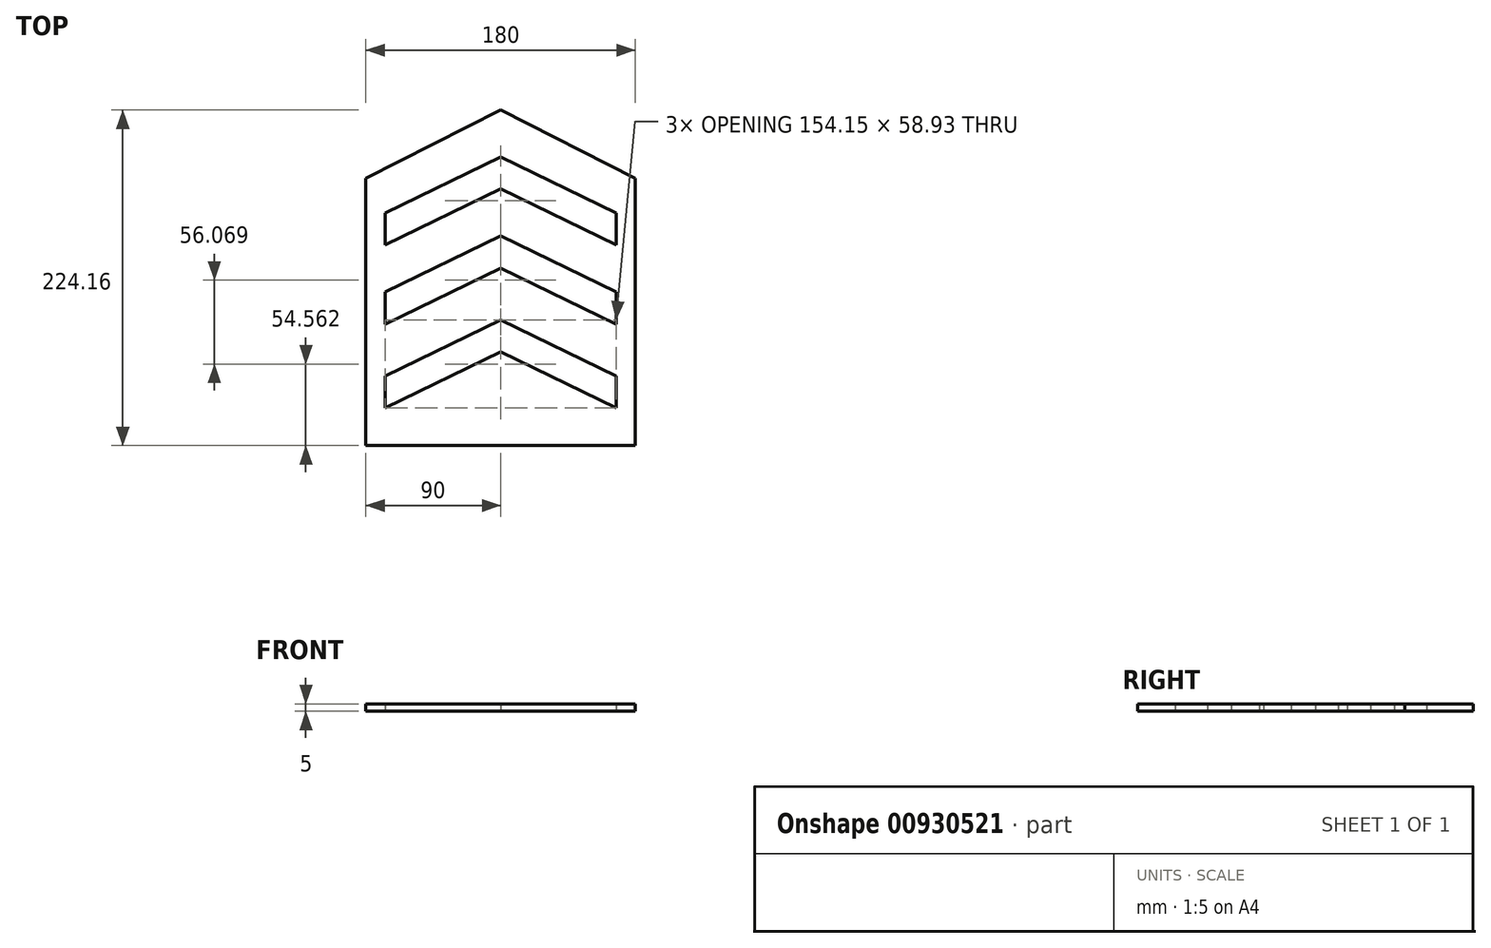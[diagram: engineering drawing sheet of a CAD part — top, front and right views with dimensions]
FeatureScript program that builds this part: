
annotation { "Feature Type Name" : "Feature", "Feature Type Description" : "" }
export const myFeature = defineFeature(function(context is Context, id is Id, definition is map)
    precondition{}
    {
        {
            var Q0;
            Q0=qCreatedBy(makeId("Top.planeOp"),FACE);
            var sketch = newSketch(context, id + "F0", { "sketchPlane" : qUnion([Q0])});
            skLineSegment(sketch, "E0", {"start": v(-447.88, 40.18) * mm, "end": v(-357.88, 85.93) * mm});
            skLineSegment(sketch, "E1", {"start": v(-447.88, 40.18) * mm, "end": v(-447.88, -138.23) * mm});
            skLineSegment(sketch, "E2.MirrorCS", {"start": v(-267.88, 40.18) * mm, "end": v(-357.88, 85.93) * mm});
            skLineSegment(sketch, "E3.MirrorCS", {"start": v(-267.88, 40.18) * mm, "end": v(-267.88, -138.23) * mm});
            skLineSegment(sketch, "E4", {"start": v(-447.88, -138.23) * mm, "end": v(-267.88, -138.23) * mm});
            skLineSegment(sketch, "E5.MirrorCS", {"start": v(-357.88, 54.77) * mm, "end": v(-280.8, 17.27) * mm});
            skLineSegment(sketch, "E6.MirrorCS", {"start": v(-280.8, 17.27) * mm, "end": v(-280.8, -4.16) * mm});
            skLineSegment(sketch, "E7.MirrorCS", {"start": v(-280.8, -4.16) * mm, "end": v(-357.88, 33.34) * mm});
            skLineSegment(sketch, "E8.MirrorCS", {"start": v(-357.88, 1.87) * mm, "end": v(-280.8, -35.64) * mm});
            skLineSegment(sketch, "E9.MirrorCS", {"start": v(-280.8, -57.07) * mm, "end": v(-357.88, -19.56) * mm});
            skLineSegment(sketch, "E10.MirrorCS", {"start": v(-357.88, -54.2) * mm, "end": v(-280.8, -91.7) * mm});
            skLineSegment(sketch, "E11.MirrorCS", {"start": v(-280.8, -113.13) * mm, "end": v(-357.88, -75.63) * mm});
            skLineSegment(sketch, "E12", {"start": v(-280.8, -35.64) * mm, "end": v(-280.8, -57.07) * mm});
            skLineSegment(sketch, "E13", {"start": v(-280.8, -91.7) * mm, "end": v(-280.8, -113.13) * mm});
            skLineSegment(sketch, "E14.MirrorCS", {"start": v(-357.88, 54.77) * mm, "end": v(-434.95, 17.27) * mm});
            skLineSegment(sketch, "E15.MirrorCS", {"start": v(-434.95, -4.16) * mm, "end": v(-357.88, 33.34) * mm});
            skLineSegment(sketch, "E16.MirrorCS", {"start": v(-434.95, 17.27) * mm, "end": v(-434.95, -4.16) * mm});
            skLineSegment(sketch, "E17.MirrorCS", {"start": v(-357.88, 1.87) * mm, "end": v(-434.95, -35.64) * mm});
            skLineSegment(sketch, "E18.MirrorCS", {"start": v(-434.95, -57.07) * mm, "end": v(-357.88, -19.56) * mm});
            skLineSegment(sketch, "E19.MirrorCS", {"start": v(-434.95, -35.64) * mm, "end": v(-434.95, -57.07) * mm});
            skLineSegment(sketch, "E20.MirrorCS", {"start": v(-357.88, -54.2) * mm, "end": v(-434.95, -91.7) * mm});
            skLineSegment(sketch, "E21.MirrorCS", {"start": v(-434.95, -113.13) * mm, "end": v(-357.88, -75.63) * mm});
            skLineSegment(sketch, "E22.MirrorCS", {"start": v(-434.95, -91.7) * mm, "end": v(-434.95, -113.13) * mm});
            skSolve(sketch);
        }
        {
            var Q0;
            Q0 = qSketchRegion(id + "F0", true);
            extrude(context, id + "F1", {"entities" : qUnion([Q0]), "depth" : 5 * mm, "offsetDistance" : 25 * mm});
        }
    });
